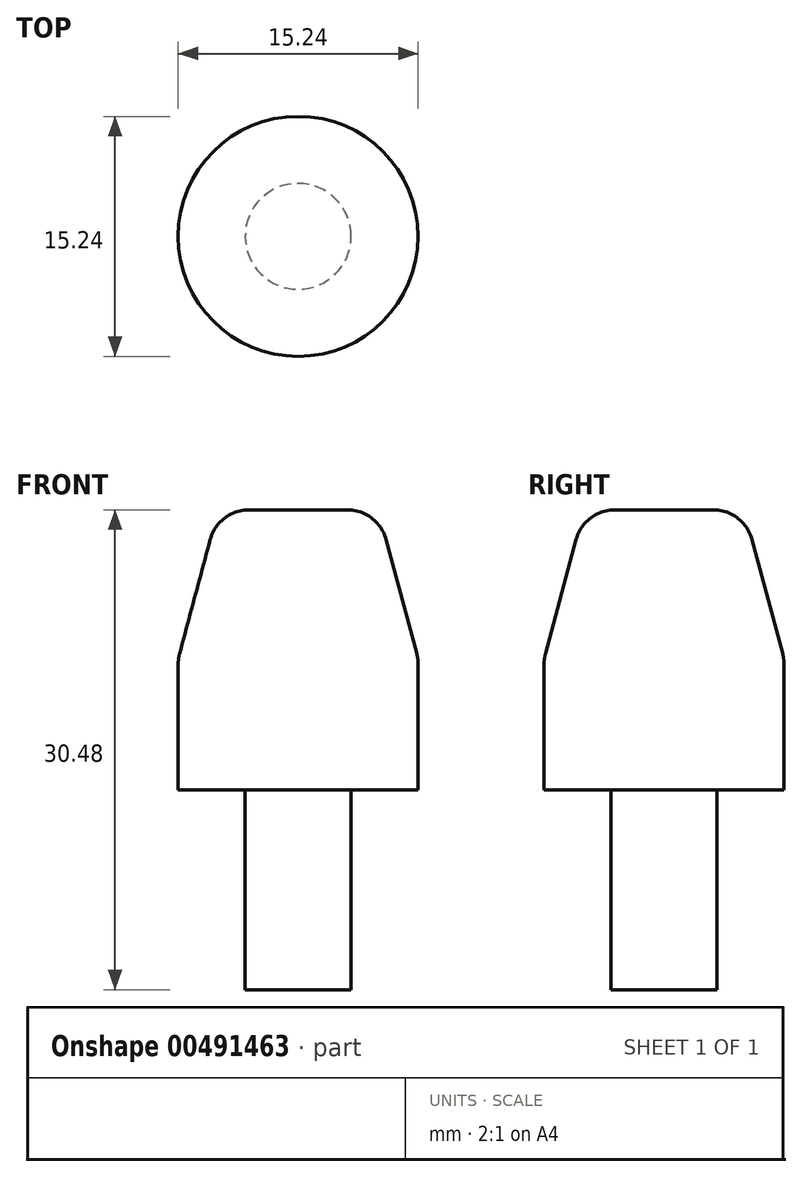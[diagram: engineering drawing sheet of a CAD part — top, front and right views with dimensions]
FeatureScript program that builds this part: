
annotation { "Feature Type Name" : "Feature", "Feature Type Description" : "" }
export const myFeature = defineFeature(function(context is Context, id is Id, definition is map)
    precondition{}
    {
        {
            var Q0;
            Q0=qCreatedBy(makeId("Top.planeOp"),FACE);
            var sketch = newSketch(context, id + "F0", { "sketchPlane" : qUnion([Q0])});
            skCircle(sketch, "E0", {"center": v(0, 0) * mm, "radius": 7.62 * mm});
            skSolve(sketch);
        }
        {
            var Q0;
            Q0=makeQuery(id+"F0.imprint","IMPRINT",FACE,{"disambiguationData":[TD([[makeQuery(id+"F0.imprint","IMPRINT",EDGE,{"derivedFrom":sQuery(id+"F0.wireOp",EDGE,"E0")}),1.0]])]});
            extrude(context, id + "F1", {"entities" : qUnion([Q0]), "depth" : 17.78 * mm});
        }
        {
            var Q0;
            Q0=makeQuery(id+"F1.opExtrude","CAP_EDGE",EDGE,{"disambiguationData":[OSD([sQuery(id+"F0.wireOp",EDGE,"E0")])],"isStart":false});
            chamfer(context, id + "F2", {"entities" : qUnion([Q0]), "chamferType" : ChamferType.OFFSET_ANGLE, "width" : 2.54 * mm, "oppositeDirection" : false, "angle" : 75 * degree, "tangentPropagation" : true});
        }
        {
            var Q0;
            {var subQ0=sQuery(id+"F0.wireOp",EDGE,"E0");Q0=makeQuery(id+"F2.opChamfer","BLEND_EDGE",EDGE,{"blendedFrom":[makeQuery(id+"F1.opExtrude","CAP_EDGE",EDGE,{"disambiguationData":[OSD([subQ0])],"isStart":false}),makeQuery(id+"F1.opExtrude","CAP_FACE",FACE,{"disambiguationData":[OSD([subQ0])],"isStart":false})],"blendedInto":[makeQuery(id+"F1.opExtrude","CAP_FACE",FACE,{"disambiguationData":[OSD([subQ0])],"isStart":false})]});}
            var Q1;
            {var subQ0=sQuery(id+"F0.wireOp",EDGE,"E0");Q1=makeQuery(id+"F2.opChamfer","BLEND_EDGE",EDGE,{"blendedFrom":[makeQuery(id+"F1.opExtrude","CAP_EDGE",EDGE,{"disambiguationData":[OSD([subQ0])],"isStart":false}),makeQuery(id+"F1.opExtrude","SWEPT_FACE",FACE,{"disambiguationData":[OSD([subQ0])]})],"blendedInto":[makeQuery(id+"F1.opExtrude","SWEPT_FACE",FACE,{"disambiguationData":[OSD([subQ0])]})]});}
            fillet(context, id + "F3", {"entities" : qUnion([Q0, Q1]), "radius" : 2.54 * mm, "tangentPropagation" : true, "allowEdgeOverflow" : false});
        }
        {
            var Q0;
            Q0=makeQuery(id+"F1.opExtrude","CAP_FACE",FACE,{"disambiguationData":[OSD([sQuery(id+"F0.wireOp",EDGE,"E0")])],"isStart":true});
            var sketch = newSketch(context, id + "F4", { "sketchPlane" : qUnion([Q0])});
            skCircle(sketch, "E1", {"center": v(0, 0) * mm, "radius": 3.37 * mm});
            skSolve(sketch);
        }
        {
            var Q0;
            Q0=makeQuery(id+"F4.imprint","IMPRINT",FACE,{"disambiguationData":[TD([[makeQuery(id+"F4.imprint","IMPRINT",EDGE,{"derivedFrom":sQuery(id+"F4.wireOp",EDGE,"E1")}),1.0]])]});
            extrude(context, id + "F5", {"entities" : qUnion([Q0]), "operationType" : NewBodyOperationType.ADD, "depth" : 12.7 * mm});
        }
    });
